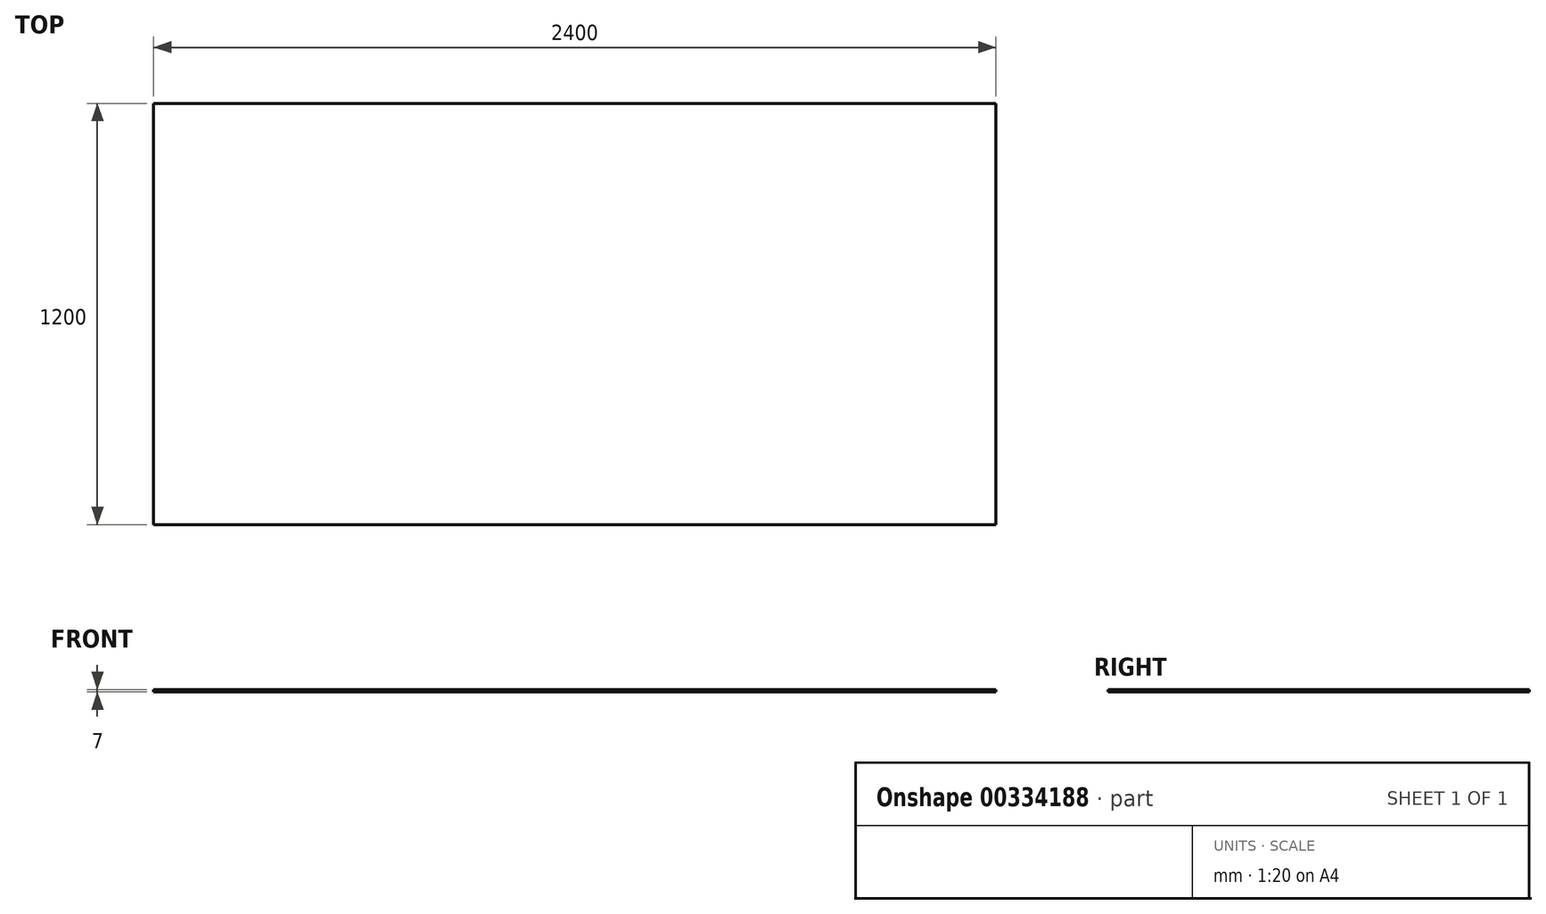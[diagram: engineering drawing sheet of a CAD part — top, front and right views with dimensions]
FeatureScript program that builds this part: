
annotation { "Feature Type Name" : "Feature", "Feature Type Description" : "" }
export const myFeature = defineFeature(function(context is Context, id is Id, definition is map)
    precondition{}
    {
        {
            var Q0;
            Q0=qCreatedBy(makeId("Front.planeOp"),FACE);
            var sketch = newSketch(context, id + "F0", { "sketchPlane" : qUnion([Q0])});
            skLineSegment(sketch, "E0.bottom", {"start": v(1200, -3.5) * mm, "end": v(-1200, -3.5) * mm});
            skLineSegment(sketch, "E0.top", {"start": v(1200, 3.5) * mm, "end": v(-1200, 3.5) * mm});
            skLineSegment(sketch, "E0.left", {"start": v(1200, -3.5) * mm, "end": v(1200, 3.5) * mm});
            skLineSegment(sketch, "E0.right", {"start": v(-1200, -3.5) * mm, "end": v(-1200, 3.5) * mm});
            skPoint(sketch, "E0.middle", {"position": v(0, 0) * mm});
            skSolve(sketch);
        }
        {
            var Q0;
            Q0=makeQuery(id+"F0.imprint","IMPRINT",FACE,{"disambiguationData":[TD([[makeQuery(id+"F0.imprint","IMPRINT",EDGE,{"derivedFrom":sQuery(id+"F0.wireOp",EDGE,"E0.bottom")}),-1.0]])]});
            extrude(context, id + "F1", {"entities" : qUnion([Q0]), "endBound" : BoundingType.SYMMETRIC, "oppositeDirection" : true, "depth" : 1200 * mm});
        }
    });
